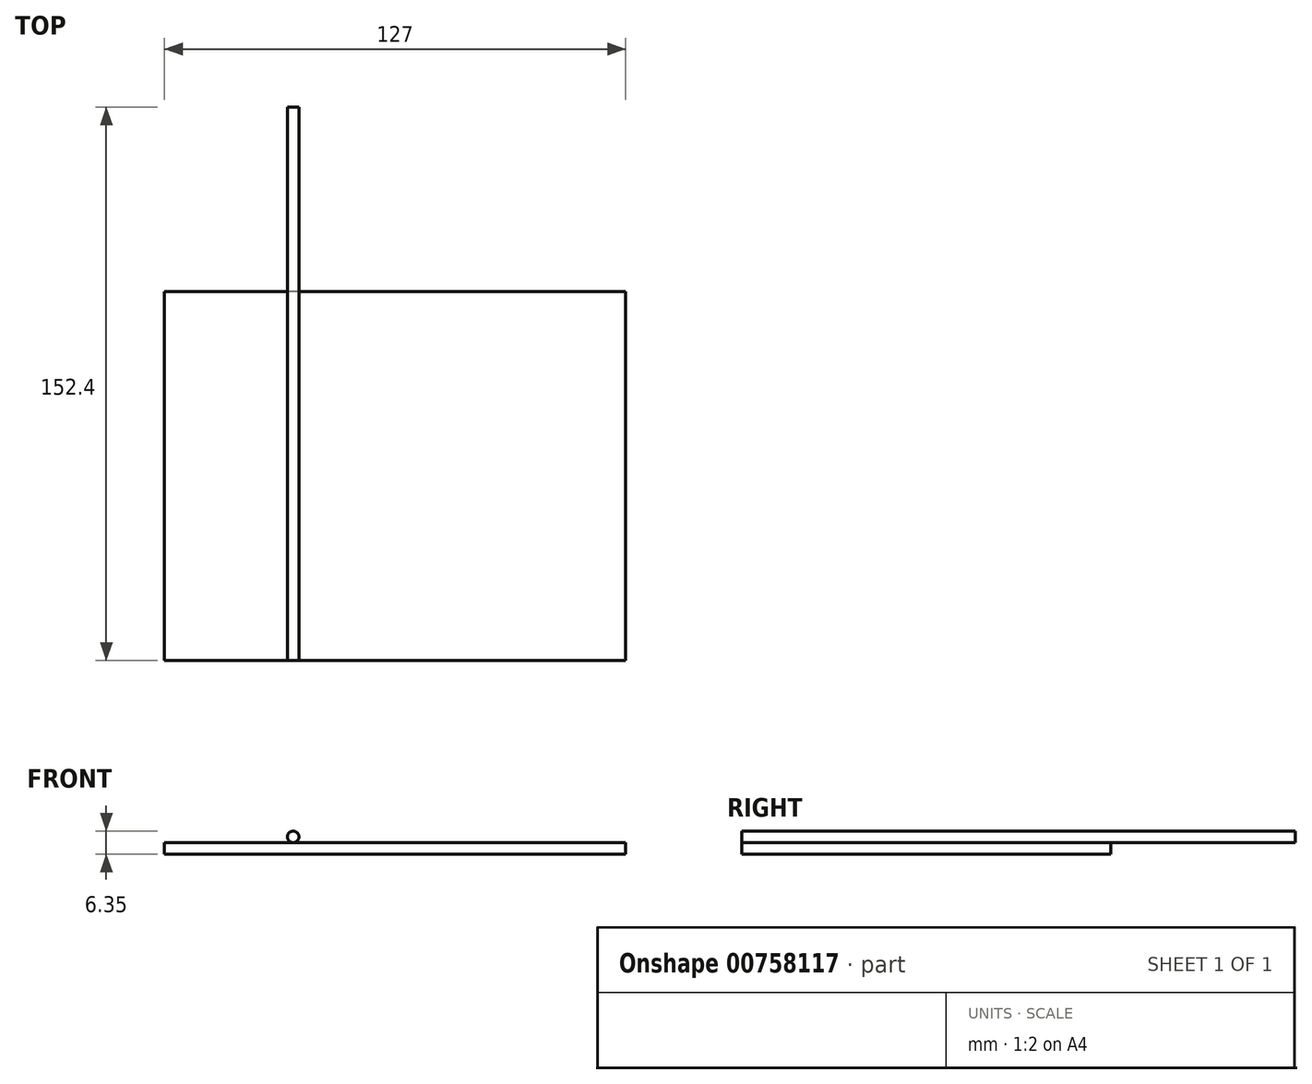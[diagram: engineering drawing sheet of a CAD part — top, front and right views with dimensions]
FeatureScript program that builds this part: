
annotation { "Feature Type Name" : "Feature", "Feature Type Description" : "" }
export const myFeature = defineFeature(function(context is Context, id is Id, definition is map)
    precondition{}
    {
        {
            var Q0;
            Q0=qCreatedBy(makeId("Top.planeOp"),FACE);
            var sketch = newSketch(context, id + "F0", { "sketchPlane" : qUnion([Q0])});
            skLineSegment(sketch, "E0.bottom", {"start": v(0, 0) * mm, "end": v(-127, 0) * mm});
            skLineSegment(sketch, "E0.top", {"start": v(0, 101.6) * mm, "end": v(-127, 101.6) * mm});
            skLineSegment(sketch, "E0.left", {"start": v(0, 0) * mm, "end": v(0, 101.6) * mm});
            skLineSegment(sketch, "E0.right", {"start": v(-127, 0) * mm, "end": v(-127, 101.6) * mm});
            skSolve(sketch);
        }
        {
            var Q0;
            Q0=makeQuery(id+"F0.imprint","IMPRINT",FACE,{"disambiguationData":[TD([[makeQuery(id+"F0.imprint","IMPRINT",EDGE,{"derivedFrom":sQuery(id+"F0.wireOp",EDGE,"E0.bottom")}),-1.0]])]});
            extrude(context, id + "F1", {"entities" : qUnion([Q0]), "depth" : 3.17 * mm, "offsetDistance" : 25.4 * mm});
        }
        {
            var Q0;
            Q0=makeQuery(id+"F1.opExtrude","SWEPT_FACE",FACE,{"disambiguationData":[OSD([sQuery(id+"F0.wireOp",EDGE,"E0.bottom")])]});
            var sketch = newSketch(context, id + "F2", { "sketchPlane" : qUnion([Q0])});
            skCircle(sketch, "E1", {"center": v(-91.56, 4.76) * mm, "radius": 1.59 * mm});
            skSolve(sketch);
        }
        {
            var Q0;
            Q0=makeQuery(id+"F2.imprint","IMPRINT",FACE,{"disambiguationData":[TD([[makeQuery(id+"F2.imprint","IMPRINT",EDGE,{"derivedFrom":sQuery(id+"F2.wireOp",EDGE,"E1")}),1.0]])]});
            extrude(context, id + "F3", {"entities" : qUnion([Q0]), "oppositeDirection" : true, "depth" : 152.4 * mm, "offsetDistance" : 25.4 * mm});
        }
    });
